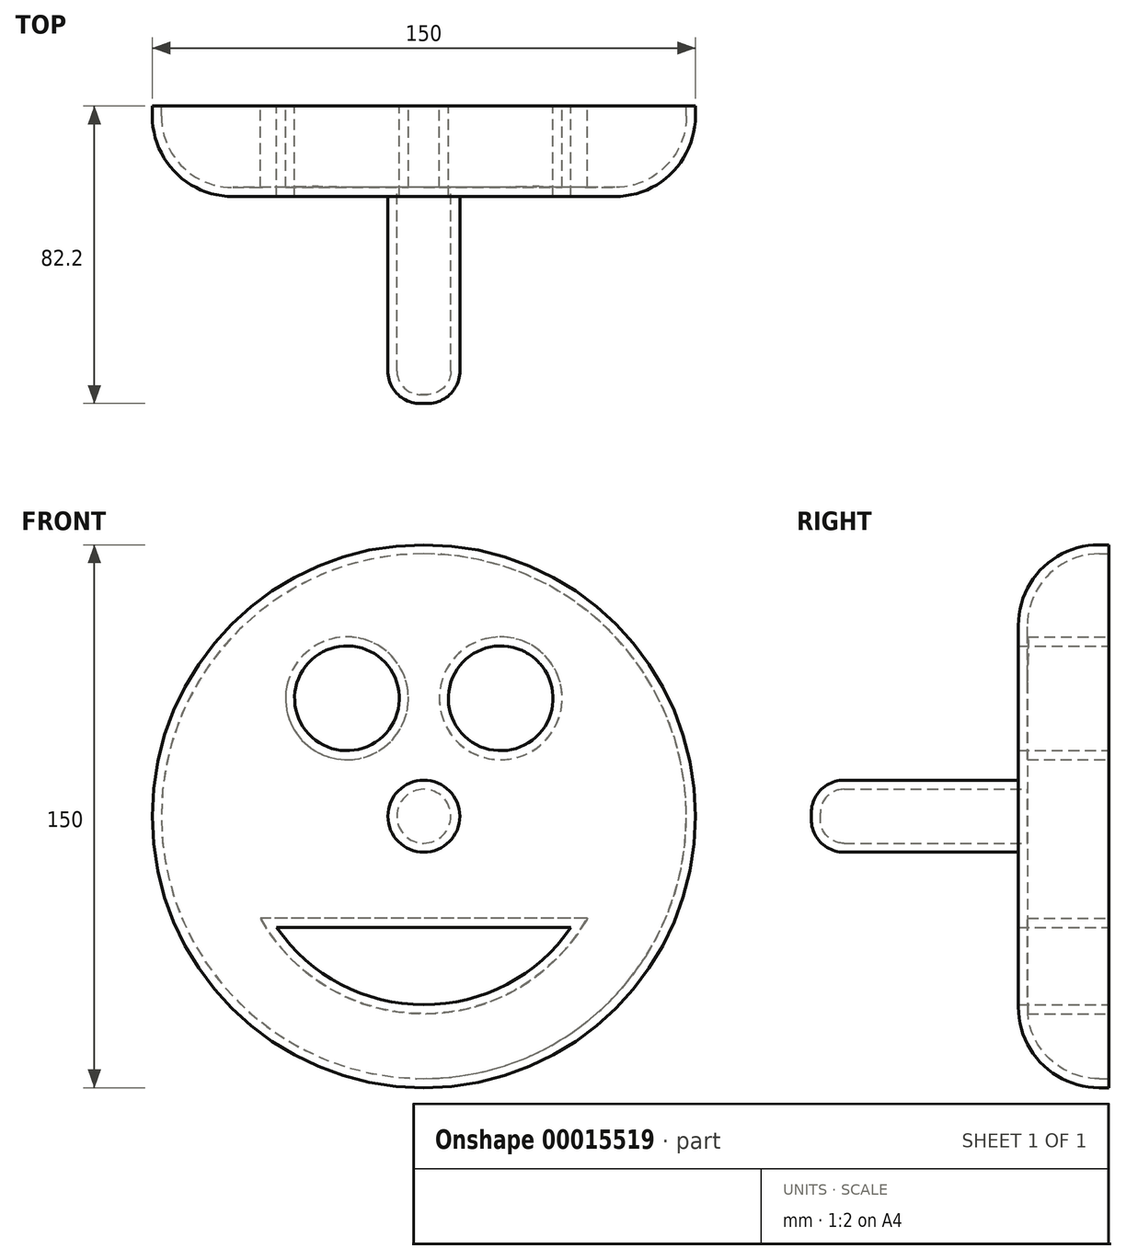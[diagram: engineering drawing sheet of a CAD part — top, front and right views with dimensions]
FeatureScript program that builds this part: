
annotation { "Feature Type Name" : "Feature", "Feature Type Description" : "" }
export const myFeature = defineFeature(function(context is Context, id is Id, definition is map)
    precondition{}
    {
        {
            var Q0;
            Q0=qCreatedBy(makeId("Front.planeOp"),FACE);
            var sketch = newSketch(context, id + "F0", { "sketchPlane" : qUnion([Q0])});
            skCircle(sketch, "E0", {"center": v(0, 0) * mm, "radius": 75 * mm});
            skCircle(sketch, "E1", {"center": v(-21.22, 32.57) * mm, "radius": 14.46 * mm});
            skLineSegment(sketch, "E2", {"start": v(0, 0) * mm, "end": v(0, 86.38) * mm, "construction": true});
            skCircle(sketch, "E3.MirrorC", {"center": v(21.22, 32.57) * mm, "radius": 14.46 * mm});
            skLineSegment(sketch, "E4", {"start": v(0, -30.73) * mm, "end": v(40.63, -30.73) * mm});
            skLineSegment(sketch, "E5.MirrorCS", {"start": v(0, -61.47) * mm, "end": v(0, -147.85) * mm, "construction": true});
            skLineSegment(sketch, "E6.MirrorCS", {"start": v(0, -30.73) * mm, "end": v(-40.63, -30.73) * mm});
            skArc(sketch, "E7", {"start": v(-40.63, -30.73) * mm, "mid": v(0, -52.1) * mm, "end": v(40.63, -30.73) * mm});
            skSolve(sketch);
        }
        {
            var Q0;
            Q0=makeQuery(id+"F0.imprint","IMPRINT",FACE,{"disambiguationData":[TD([[makeQuery(id+"F0.imprint","IMPRINT",EDGE,{"derivedFrom":sQuery(id+"F0.wireOp",EDGE,"E0")}),1.0]])]});
            extrude(context, id + "F1", {"entities" : qUnion([Q0]), "depth" : 25 * mm});
        }
        {
            var Q0;
            Q0=makeQuery(id+"F1.opExtrude","CAP_FACE",FACE,{"disambiguationData":[OSD([sQuery(id+"F0.wireOp",EDGE,"E0"),sQuery(id+"F0.wireOp",EDGE,"E1"),sQuery(id+"F0.wireOp",EDGE,"E3.MirrorC"),sQuery(id+"F0.wireOp",EDGE,"E4"),sQuery(id+"F0.wireOp",EDGE,"E6.MirrorCS"),sQuery(id+"F0.wireOp",EDGE,"E7")])],"isStart":false});
            var sketch = newSketch(context, id + "F2", { "sketchPlane" : qUnion([Q0])});
            skCircle(sketch, "E8", {"center": v(0, 0) * mm, "radius": 9.94 * mm});
            skSolve(sketch);
        }
        {
            var Q0;
            Q0=makeQuery(id+"F2.imprint","IMPRINT",FACE,{"disambiguationData":[TD([[makeQuery(id+"F2.imprint","IMPRINT",EDGE,{"derivedFrom":sQuery(id+"F2.wireOp",EDGE,"E8")}),1.0]])]});
            extrude(context, id + "F3", {"entities" : qUnion([Q0]), "operationType" : NewBodyOperationType.ADD, "depth" : 57.2 * mm});
        }
        {
            var Q0;
            Q0=makeQuery(id+"F3.opExtrude","CAP_EDGE",EDGE,{"disambiguationData":[OSD([sQuery(id+"F2.wireOp",EDGE,"E8")])],"isStart":false});
            fillet(context, id + "F4", {"entities" : qUnion([Q0]), "radius" : 9 * mm, "tangentPropagation" : true, "allowEdgeOverflow" : false});
        }
        {
            var Q0;
            Q0=makeQuery(id+"F1.opExtrude","CAP_EDGE",EDGE,{"disambiguationData":[OSD([sQuery(id+"F0.wireOp",EDGE,"E0")])],"isStart":false});
            fillet(context, id + "F5", {"entities" : qUnion([Q0]), "radius" : 22.26 * mm, "tangentPropagation" : true, "allowEdgeOverflow" : false});
        }
        {
            var Q0;
            Q0=makeQuery(id+"F1.opExtrude","CAP_FACE",FACE,{"disambiguationData":[OSD([sQuery(id+"F0.wireOp",EDGE,"E0"),sQuery(id+"F0.wireOp",EDGE,"E1"),sQuery(id+"F0.wireOp",EDGE,"E3.MirrorC"),sQuery(id+"F0.wireOp",EDGE,"E4"),sQuery(id+"F0.wireOp",EDGE,"E6.MirrorCS"),sQuery(id+"F0.wireOp",EDGE,"E7")])],"isStart":true});
            shell(context, id + "F6", {"entities" : qUnion([Q0]), "thickness" : 2.5 * mm});
        }
    });
